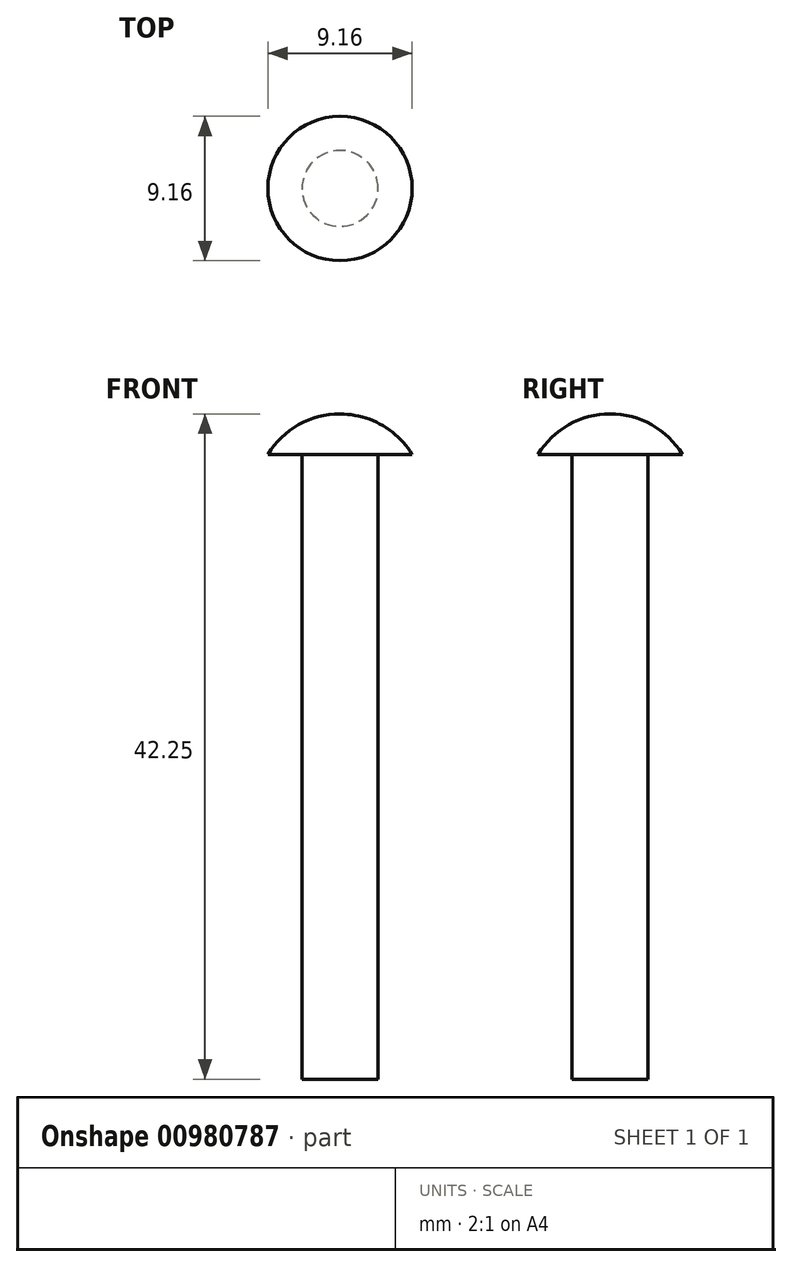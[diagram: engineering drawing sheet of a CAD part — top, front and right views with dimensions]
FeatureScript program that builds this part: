
annotation { "Feature Type Name" : "Feature", "Feature Type Description" : "" }
export const myFeature = defineFeature(function(context is Context, id is Id, definition is map)
    precondition{}
    {
        {
            var Q0;
            Q0=qCreatedBy(makeId("Front.planeOp"),FACE);
            var sketch = newSketch(context, id + "F0", { "sketchPlane" : qUnion([Q0])});
            skLineSegment(sketch, "E0", {"start": v(0, 39.69) * mm, "end": v(0, 0) * mm});
            skLineSegment(sketch, "E1", {"start": v(0, 0) * mm, "end": v(-2.41, 0) * mm});
            skLineSegment(sketch, "E2", {"start": v(-2.41, 0) * mm, "end": v(-2.41, 39.69) * mm});
            skLineSegment(sketch, "E3", {"start": v(-2.41, 39.69) * mm, "end": v(-4.58, 39.69) * mm});
            skArc(sketch, "E4", {"start": v(0, 42.25) * mm, "mid": v(-2.63, 41.57) * mm, "end": v(-4.58, 39.69) * mm});
            skLineSegment(sketch, "E5", {"start": v(0, 42.25) * mm, "end": v(4.27, 42.25) * mm, "construction": true});
            skLineSegment(sketch, "E6", {"start": v(0, 42.25) * mm, "end": v(0, 39.69) * mm});
            skSolve(sketch);
        }
        {
            var Q0;
            Q0=qSketchRegion(id+"F0",true);
            var Q1;
            Q1=sQuery(id+"F0.wireOp",EDGE,"E0");
            revolve(context, id + "F1", {"surfaceOperationType" : NewSurfaceOperationType.NEW, "entities" : qUnion([Q0]), "axis" : qUnion([Q1]), "revolveType" : RevolveType.FULL});
        }
    });
